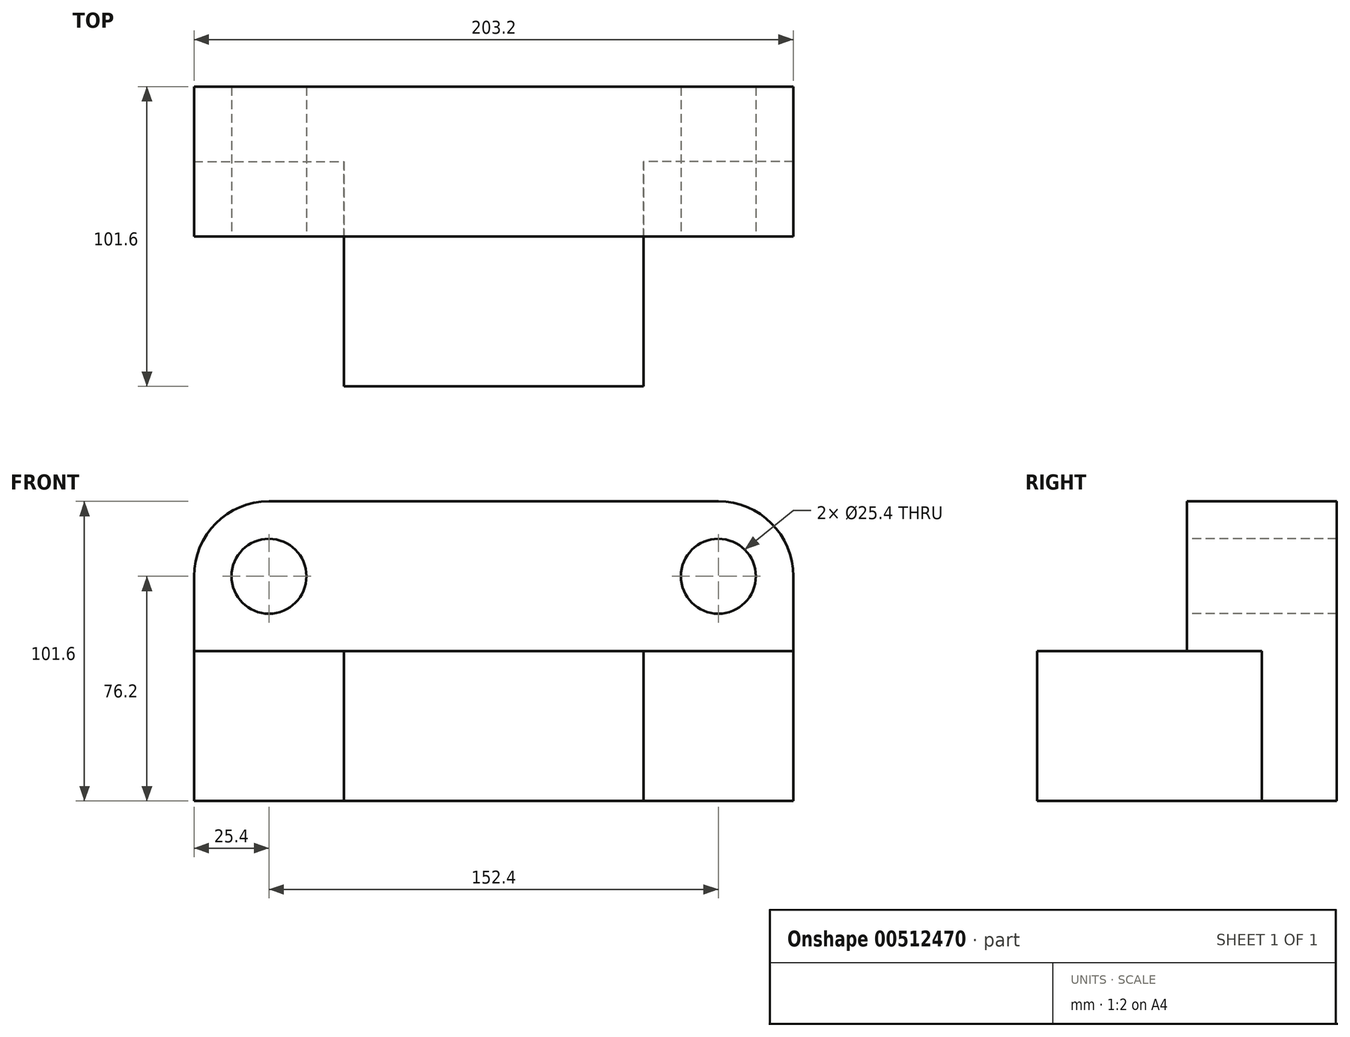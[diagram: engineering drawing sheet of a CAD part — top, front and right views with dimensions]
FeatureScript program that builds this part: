
annotation { "Feature Type Name" : "Feature", "Feature Type Description" : "" }
export const myFeature = defineFeature(function(context is Context, id is Id, definition is map)
    precondition{}
    {
        {
            var Q0;
            Q0=qCreatedBy(makeId("Front.planeOp"),FACE);
            var sketch = newSketch(context, id + "F0", { "sketchPlane" : qUnion([Q0])});
            skLineSegment(sketch, "E0.bottom", {"start": v(0, 0) * mm, "end": v(101.6, 0) * mm});
            skLineSegment(sketch, "E0.top", {"start": v(0, 50.8) * mm, "end": v(101.6, 50.8) * mm});
            skLineSegment(sketch, "E0.left", {"start": v(0, 0) * mm, "end": v(0, 50.8) * mm});
            skLineSegment(sketch, "E0.right", {"start": v(101.6, 0) * mm, "end": v(101.6, 50.8) * mm});
            skSolve(sketch);
        }
        {
            var Q0;
            Q0=makeQuery(id+"F0.imprint","IMPRINT",FACE,{"disambiguationData":[TD([[makeQuery(id+"F0.imprint","IMPRINT",EDGE,{"derivedFrom":sQuery(id+"F0.wireOp",EDGE,"E0.bottom")}),1.0]])]});
            extrude(context, id + "F1", {"entities" : qUnion([Q0]), "depth" : 101.6 * mm, "offsetDistance" : 25.4 * mm});
        }
        {
            var Q0;
            Q0=makeQuery(id+"F1.opExtrude","SWEPT_FACE",FACE,{"disambiguationData":[OSD([sQuery(id+"F0.wireOp",EDGE,"E0.top")])]});
            var sketch = newSketch(context, id + "F2", { "sketchPlane" : qUnion([Q0])});
            skLineSegment(sketch, "E1.bottom", {"start": v(0, 0) * mm, "end": v(101.6, 0) * mm});
            skLineSegment(sketch, "E1.top", {"start": v(0, -50.8) * mm, "end": v(101.6, -50.8) * mm});
            skLineSegment(sketch, "E1.left", {"start": v(0, 0) * mm, "end": v(0, -50.8) * mm});
            skLineSegment(sketch, "E1.right", {"start": v(101.6, 0) * mm, "end": v(101.6, -50.8) * mm});
            skSolve(sketch);
        }
        {
            var Q0;
            Q0=makeQuery(id+"F2.imprint","IMPRINT",FACE,{"disambiguationData":[TD([[makeQuery(id+"F2.imprint","IMPRINT",EDGE,{"derivedFrom":sQuery(id+"F2.wireOp",EDGE,"E1.bottom")}),-1.0]])]});
            extrude(context, id + "F3", {"entities" : qUnion([Q0]), "operationType" : NewBodyOperationType.ADD, "depth" : 50.8 * mm, "offsetDistance" : 25.4 * mm});
        }
        {
            var Q0;
            Q0=makeQuery(id+"F3.boolean.opBoolean","MERGE",FACE,{"derivedFrom":[makeQuery(id+"F1.opExtrude","SWEPT_FACE",FACE,{"disambiguationData":[OSD([sQuery(id+"F0.wireOp",EDGE,"E0.right")])]}),makeQuery(id+"F3.opExtrude","SWEPT_FACE",FACE,{"disambiguationData":[OSD([sQuery(id+"F2.wireOp",EDGE,"E1.right")])]})]});
            var sketch = newSketch(context, id + "F4", { "sketchPlane" : qUnion([Q0])});
            skLineSegment(sketch, "E2.bottom", {"start": v(0, 0) * mm, "end": v(-25.4, 0) * mm});
            skLineSegment(sketch, "E2.top", {"start": v(0, 50.8) * mm, "end": v(-25.4, 50.8) * mm});
            skLineSegment(sketch, "E2.left", {"start": v(0, 0) * mm, "end": v(0, 50.8) * mm});
            skLineSegment(sketch, "E2.right", {"start": v(-25.4, 0) * mm, "end": v(-25.4, 50.8) * mm});
            skSolve(sketch);
        }
        {
            var Q0;
            Q0=makeQuery(id+"F4.imprint","IMPRINT",FACE,{"disambiguationData":[TD([[makeQuery(id+"F4.imprint","IMPRINT",EDGE,{"derivedFrom":sQuery(id+"F4.wireOp",EDGE,"E2.bottom")}),1.0]])]});
            extrude(context, id + "F5", {"entities" : qUnion([Q0]), "operationType" : NewBodyOperationType.ADD, "depth" : 50.8 * mm, "offsetDistance" : 25.4 * mm});
        }
        {
            var Q0;
            Q0=makeQuery(id+"F3.boolean.opBoolean","MERGE",FACE,{"derivedFrom":[makeQuery(id+"F1.opExtrude","SWEPT_FACE",FACE,{"disambiguationData":[OSD([sQuery(id+"F0.wireOp",EDGE,"E0.right")])]}),makeQuery(id+"F3.opExtrude","SWEPT_FACE",FACE,{"disambiguationData":[OSD([sQuery(id+"F2.wireOp",EDGE,"E1.right")])]})]});
            var sketch = newSketch(context, id + "F6", { "sketchPlane" : qUnion([Q0])});
            skLineSegment(sketch, "E3.bottom", {"start": v(0, 101.6) * mm, "end": v(-50.8, 101.6) * mm});
            skLineSegment(sketch, "E3.top", {"start": v(0, 50.8) * mm, "end": v(-50.8, 50.8) * mm});
            skLineSegment(sketch, "E3.left", {"start": v(0, 101.6) * mm, "end": v(0, 50.8) * mm});
            skLineSegment(sketch, "E3.right", {"start": v(-50.8, 101.6) * mm, "end": v(-50.8, 50.8) * mm});
            skSolve(sketch);
        }
        {
            var Q0;
            Q0=makeQuery(id+"F6.imprint","IMPRINT",FACE,{"disambiguationData":[TD([[makeQuery(id+"F6.imprint","IMPRINT",EDGE,{"derivedFrom":sQuery(id+"F6.wireOp",EDGE,"E3.bottom")}),-1.0]])]});
            extrude(context, id + "F7", {"entities" : qUnion([Q0]), "operationType" : NewBodyOperationType.ADD, "depth" : 50.8 * mm, "offsetDistance" : 25.4 * mm});
        }
        {
            var Q0;
            Q0=makeQuery(id+"F7.opExtrude","CAP_EDGE",EDGE,{"disambiguationData":[OSD([sQuery(id+"F6.wireOp",EDGE,"E3.bottom")])],"isStart":false});
            fillet(context, id + "F8", {"entities" : qUnion([Q0]), "radius" : 25.4 * mm, "tangentPropagation" : true, "allowEdgeOverflow" : false});
        }
        {
            var Q0;
            Q0=makeQuery(id+"F3.boolean.opBoolean","MERGE",FACE,{"derivedFrom":[makeQuery(id+"F1.opExtrude","SWEPT_FACE",FACE,{"disambiguationData":[OSD([sQuery(id+"F0.wireOp",EDGE,"E0.left")])]}),makeQuery(id+"F3.opExtrude","SWEPT_FACE",FACE,{"disambiguationData":[OSD([sQuery(id+"F2.wireOp",EDGE,"E1.left")])]})]});
            var sketch = newSketch(context, id + "F9", { "sketchPlane" : qUnion([Q0])});
            skLineSegment(sketch, "E4.bottom", {"start": v(0, 0) * mm, "end": v(25.4, 0) * mm});
            skLineSegment(sketch, "E4.top", {"start": v(0, 50.8) * mm, "end": v(25.4, 50.8) * mm});
            skLineSegment(sketch, "E4.left", {"start": v(0, 0) * mm, "end": v(0, 50.8) * mm});
            skLineSegment(sketch, "E4.right", {"start": v(25.4, 0) * mm, "end": v(25.4, 50.8) * mm});
            skSolve(sketch);
        }
        {
            var Q0;
            Q0=makeQuery(id+"F9.imprint","IMPRINT",FACE,{"disambiguationData":[TD([[makeQuery(id+"F9.imprint","IMPRINT",EDGE,{"derivedFrom":sQuery(id+"F9.wireOp",EDGE,"E4.bottom")}),-1.0]])]});
            extrude(context, id + "F10", {"entities" : qUnion([Q0]), "operationType" : NewBodyOperationType.ADD, "depth" : 50.8 * mm, "offsetDistance" : 25.4 * mm});
        }
        {
            var Q0;
            Q0=makeQuery(id+"F3.boolean.opBoolean","MERGE",FACE,{"derivedFrom":[makeQuery(id+"F1.opExtrude","SWEPT_FACE",FACE,{"disambiguationData":[OSD([sQuery(id+"F0.wireOp",EDGE,"E0.left")])]}),makeQuery(id+"F3.opExtrude","SWEPT_FACE",FACE,{"disambiguationData":[OSD([sQuery(id+"F2.wireOp",EDGE,"E1.left")])]})]});
            var sketch = newSketch(context, id + "F11", { "sketchPlane" : qUnion([Q0])});
            skLineSegment(sketch, "E5.bottom", {"start": v(0, 101.6) * mm, "end": v(50.8, 101.6) * mm});
            skLineSegment(sketch, "E5.top", {"start": v(0, 50.8) * mm, "end": v(50.8, 50.8) * mm});
            skLineSegment(sketch, "E5.left", {"start": v(0, 101.6) * mm, "end": v(0, 50.8) * mm});
            skLineSegment(sketch, "E5.right", {"start": v(50.8, 101.6) * mm, "end": v(50.8, 50.8) * mm});
            skSolve(sketch);
        }
        {
            var Q0;
            Q0=makeQuery(id+"F11.imprint","IMPRINT",FACE,{"disambiguationData":[TD([[makeQuery(id+"F11.imprint","IMPRINT",EDGE,{"derivedFrom":sQuery(id+"F11.wireOp",EDGE,"E5.bottom")}),1.0]])]});
            extrude(context, id + "F12", {"entities" : qUnion([Q0]), "operationType" : NewBodyOperationType.ADD, "depth" : 50.8 * mm, "offsetDistance" : 25.4 * mm});
        }
        {
            var Q0;
            Q0=makeQuery(id+"F12.opExtrude","CAP_EDGE",EDGE,{"disambiguationData":[OSD([sQuery(id+"F11.wireOp",EDGE,"E5.bottom")])],"isStart":false});
            fillet(context, id + "F13", {"entities" : qUnion([Q0]), "radius" : 25.4 * mm, "tangentPropagation" : true, "allowEdgeOverflow" : false});
        }
        {
            var Q0;
            Q0=makeQuery(id+"F12.boolean.opBoolean","MERGE",FACE,{"derivedFrom":[makeQuery(id+"F7.boolean.opBoolean","MERGE",FACE,{"derivedFrom":[makeQuery(id+"F3.opExtrude","SWEPT_FACE",FACE,{"disambiguationData":[OSD([sQuery(id+"F2.wireOp",EDGE,"E1.top")])]}),makeQuery(id+"F7.opExtrude","SWEPT_FACE",FACE,{"disambiguationData":[OSD([sQuery(id+"F6.wireOp",EDGE,"E3.right")])]})]}),makeQuery(id+"F12.opExtrude","SWEPT_FACE",FACE,{"disambiguationData":[OSD([sQuery(id+"F11.wireOp",EDGE,"E5.right")])]})]});
            var sketch = newSketch(context, id + "F14", { "sketchPlane" : qUnion([Q0])});
            skCircle(sketch, "E6", {"center": v(-25.4, 76.2) * mm, "radius": 12.7 * mm});
            skSolve(sketch);
        }
        {
            var Q0;
            Q0=makeQuery(id+"F14.imprint","IMPRINT",FACE,{"disambiguationData":[TD([[makeQuery(id+"F14.imprint","IMPRINT",EDGE,{"derivedFrom":sQuery(id+"F14.wireOp",EDGE,"E6")}),1.0]])]});
            extrude(context, id + "F15", {"entities" : qUnion([Q0]), "operationType" : NewBodyOperationType.REMOVE, "oppositeDirection" : true, "depth" : 101.6 * mm, "offsetDistance" : 25.4 * mm});
        }
        {
            var Q0;
            Q0=makeQuery(id+"F12.boolean.opBoolean","MERGE",FACE,{"derivedFrom":[makeQuery(id+"F7.boolean.opBoolean","MERGE",FACE,{"derivedFrom":[makeQuery(id+"F3.opExtrude","SWEPT_FACE",FACE,{"disambiguationData":[OSD([sQuery(id+"F2.wireOp",EDGE,"E1.top")])]}),makeQuery(id+"F7.opExtrude","SWEPT_FACE",FACE,{"disambiguationData":[OSD([sQuery(id+"F6.wireOp",EDGE,"E3.right")])]})]}),makeQuery(id+"F12.opExtrude","SWEPT_FACE",FACE,{"disambiguationData":[OSD([sQuery(id+"F11.wireOp",EDGE,"E5.right")])]})]});
            var sketch = newSketch(context, id + "F16", { "sketchPlane" : qUnion([Q0])});
            skCircle(sketch, "E7", {"center": v(127, 76.2) * mm, "radius": 12.7 * mm});
            skSolve(sketch);
        }
        {
            var Q0;
            Q0=makeQuery(id+"F16.imprint","IMPRINT",FACE,{"disambiguationData":[TD([[makeQuery(id+"F16.imprint","IMPRINT",EDGE,{"derivedFrom":sQuery(id+"F16.wireOp",EDGE,"E7")}),1.0]])]});
            extrude(context, id + "F17", {"entities" : qUnion([Q0]), "operationType" : NewBodyOperationType.REMOVE, "oppositeDirection" : true, "depth" : 101.6 * mm, "offsetDistance" : 25.4 * mm});
        }
    });
